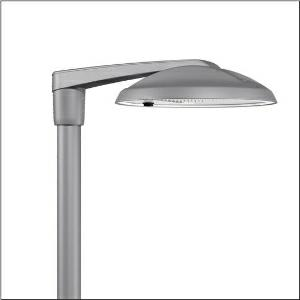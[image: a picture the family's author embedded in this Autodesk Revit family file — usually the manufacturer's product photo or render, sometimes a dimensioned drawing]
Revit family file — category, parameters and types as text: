
# Revit family: dl_50_iq_mini___st1_0a_5xa248d31u08ne_582b
name_source: partatom
category: Lighting Fixtures
units: mm (PartAtom-declared; Revit-internal decimal feet)

## family parameters
Cut with Voids When Loaded = No
Host = Face
Light Source = No
Part Type = Normal
Room Calculation Point = No
Round Connector Dimension = Use Diameter
Shared = No

## types (1)
- --- (1 x LED, 17900 lm, 110.1 W, 3000K)
    Apparent Load = 110 VA
    CIE Flux Codes = 37 72 97 100 100
    Color Rendering = 70
    Color Temperature = 3000K
    Default Elevation = 1800 mm
    Description = DL 50 iQ mini, mast luminaire, primary light control with lens, of PMMA, primary optical cover: cover, of toughened safety glass, transparent, light distribution: ST1.0a, light emission: direct distribution, primary light characteristic: asymmetric, installation type: post-top, side-entry, LED, High Power LED, rated luminous flux: 17.900lm, luminous efficacy: 163lm/W, light colour: 730, colour temperature: 3000K, control gear: iQ-Street Remote, D4i with power reduction, control: optimised constant luminous flux control (CLO 2.0), Desk-Remote (wireless, voltage-free reading and setting of iQ features in the workshop via application-optimized NFC function/RFID function), Light-Fading, Smart-Wire, Night-Set, Lumen-Switch, Temp-Guard, Auto-Match, Street-Remote, pre-setting: logarithmic dimming characteristic, mains connection: 220..240V, AC, 50/60Hz, connection cable pre-assembled, cable length: 10,5m, start of lifetime: 110W, end of service life: 116W, reduction: 50W, luminaire housing, of diecast aluminium, powder-coated, SITECO metallic grey (DB 702S), inclination adjustable: 0°, 5°, 10° (post-top) | 0°, -5°, -10°, -15° (side-entry), please order mast post-top element or mast side-entry element separately, diameter: 500mm, height: 115mm, post-top: for spigot size d x l = 76 x 100mm; with reducer (optional accessory) 60 x 100mm | side-entry: for spigot size d x l = 60 x 100mm; with reducer (optional accessory) 42 x 100mm, mounting height: 4..6m, Smart Interface below, protection rating (complete): IP66, insulation class (complete): insulation class II (safety insulation), certification: CE, ENEC, ENEC+, VDE, impact resistance: IK08, permissible operating ambient temperature for outdoor applications: -25..+40°C, standard-compliant lighting for roads and squares, packaging unit: 1 piece

Light Distribution: ST1.0a
    Height = 115 mm
    Lamp = 1 x LED
    Lamp Light Flux = 17900 lm
    Lamp Power = 110.1 W
    Lamp count = 1
    Length = 500 mm
    Luminous efficacy = 163 lm/W
    Manufacturer = Siteco
    ModVariant = No
    Model = 5XA248D31U08NE
    Number of Poles = 1
    OnlyDefault = Yes
    Power Factor = 1
    Product Name = DL 50 iQ mini | ST1.0a
    Product group = mast luminaire | pylon top
    ProductGroupID = 6100
    Protection Class = Protection class II
    Protection Degree = IP 66
    RLX_Detail_Level = 1
    RLX_Emergency_Light_Flux = 0 lm
    RLX_Emergency_Type = 0
    RLX_Emergency_Type_DB = No
    RlxData = <blob elided: 106597 chars, md5=141212ab>
    Socket = socket
    Standby Power = 0 W
    System Light Flux = 17900 lm
    System Power = 110 W
    Type Comments = factory setting: luminous flux: 100 % | dim-lin: 254 | 601 mA
    Type Image = l_1296955.jpg
    URL = http://relux.com
    VarID = @adj_072901
    Voltage = 0 V
    Weight = 0.00 kg
    Width = 0 mm  [stored 0 ft]

note: [stored X ft] marks values corroborated as IEEE doubles in the binary element streams (Revit-internal decimal feet)

## geometry (parser evidence)
native form markers: Blend x4, Sweep x9
no freeform markers — native parametric forms only
